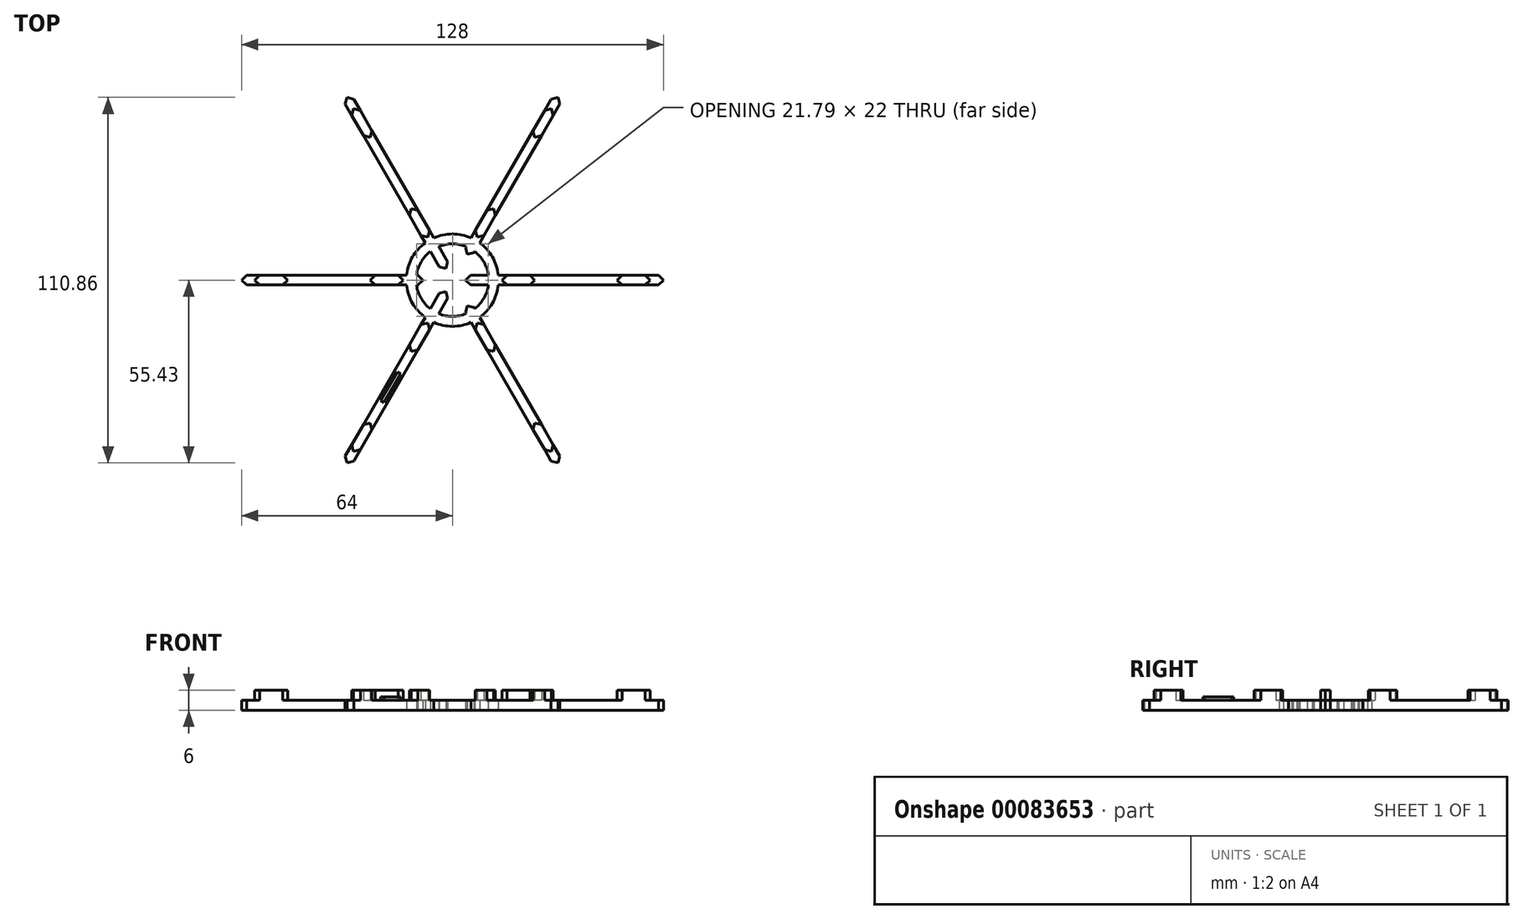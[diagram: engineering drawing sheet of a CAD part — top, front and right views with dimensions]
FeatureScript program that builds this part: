
annotation { "Feature Type Name" : "Feature", "Feature Type Description" : "" }
export const myFeature = defineFeature(function(context is Context, id is Id, definition is map)
    precondition{}
    {
        {
            var Q0;
            Q0=qCreatedBy(makeId("Top.planeOp"),FACE);
            var sketch = newSketch(context, id + "F0", { "sketchPlane" : qUnion([Q0])});
            skLineSegment(sketch, "E0", {"start": v(-51.99, 0) * mm, "end": v(34.37, 0) * mm, "construction": true});
            skLineSegment(sketch, "E1", {"start": v(-11.35, 19.65) * mm, "end": v(25.33, -43.88) * mm, "construction": true});
            skLineSegment(sketch, "E2", {"start": v(11.11, 19.25) * mm, "end": v(-29.6, -51.26) * mm, "construction": true});
            skLineSegment(sketch, "E3", {"start": v(-4.05, -4.01) * mm, "end": v(-32.55, -53.38) * mm});
            skLineSegment(sketch, "E4", {"start": v(-29.95, -54.88) * mm, "end": v(-1.45, -5.51) * mm});
            skCircle(sketch, "E5", {"center": v(0, 0) * mm, "radius": 4 * mm, "construction": true});
            skLineSegment(sketch, "E6", {"start": v(-4.05, -4.01) * mm, "end": v(-2, -3.46) * mm});
            skLineSegment(sketch, "E7", {"start": v(-2, -3.46) * mm, "end": v(-1.45, -5.51) * mm});
            skLineSegment(sketch, "E8", {"start": v(-32.55, -53.38) * mm, "end": v(-32, -55.43) * mm});
            skLineSegment(sketch, "E9", {"start": v(-32, -55.43) * mm, "end": v(-29.95, -54.88) * mm});
            skLineSegment(sketch, "E10", {"start": v(-62.5, 1.5) * mm, "end": v(-10.5, 1.5) * mm});
            skLineSegment(sketch, "E11", {"start": v(-10.5, -1.5) * mm, "end": v(-62.5, -1.5) * mm});
            skLineSegment(sketch, "E12", {"start": v(-10.5, 1.5) * mm, "end": v(-9, 0) * mm});
            skLineSegment(sketch, "E13", {"start": v(-9, 0) * mm, "end": v(-10.5, -1.5) * mm});
            skLineSegment(sketch, "E14", {"start": v(-62.5, 1.5) * mm, "end": v(-64, 0) * mm});
            skLineSegment(sketch, "E15", {"start": v(-64, 0) * mm, "end": v(-62.5, -1.5) * mm});
            skCircle(sketch, "E16", {"center": v(0, 0) * mm, "radius": 64 * mm, "construction": true});
            skSolve(sketch);
        }
        {
            var Q0;
            {var subQ0=sQuery(id+"F0.wireOp",EDGE,"c0tjFI8d-UXuB-YWxn-vJMP-8DVr5BACsfKR");var subQ1=sQuery(id+"F0.wireOp",EDGE,"E4");var subQ2=makeQuery(id+"F0.imprint","INTERSECT",VERTEX,{"derivedFrom":[subQ1,subQ0]});Q0=makeQuery(id+"F0.imprint","IMPRINT",FACE,{"disambiguationData":[TD([[makeQuery(id+"F0.imprint","IMPRINT",EDGE,{"disambiguationData":[TD([[subQ2,-1.0]])],"derivedFrom":subQ1}),-1.0]])]});}
            var Q1;
            {var subQ0=sQuery(id+"F0.wireOp",EDGE,"E6");Q1=makeQuery(id+"F0.imprint","IMPRINT",FACE,{"disambiguationData":[TD([[makeQuery(id+"F0.imprint","IMPRINT",EDGE,{"derivedFrom":subQ0}),-1.0]])]});}
            var Q2;
            {var subQ0=sQuery(id+"F0.wireOp",EDGE,"c0tjFI8d-UXuB-YWxn-vJMP-8DVr5BACsfKR");var subQ1=sQuery(id+"F0.wireOp",EDGE,"E3");var subQ2=makeQuery(id+"F0.imprint","INTERSECT",VERTEX,{"derivedFrom":[subQ1,subQ0]});Q2=makeQuery(id+"F0.imprint","IMPRINT",FACE,{"disambiguationData":[TD([[makeQuery(id+"F0.imprint","IMPRINT",EDGE,{"disambiguationData":[TD([[subQ2,1.0]])],"derivedFrom":subQ1}),1.0]])]});}
            var Q3;
            {var subQ0=sQuery(id+"F0.wireOp",EDGE,"c0tjFI8d-UXuB-YWxn-vJMP-8DVr5BACsfKR");var subQ1=sQuery(id+"F0.wireOp",EDGE,"E3");var subQ2=makeQuery(id+"F0.imprint","INTERSECT",VERTEX,{"derivedFrom":[subQ1,subQ0]});Q3=makeQuery(id+"F0.imprint","IMPRINT",FACE,{"disambiguationData":[TD([[makeQuery(id+"F0.imprint","IMPRINT",EDGE,{"disambiguationData":[TD([[subQ2,1.0]])],"derivedFrom":subQ1}),-1.0]])]});}
            var Q4;
            {var subQ0=sQuery(id+"F0.wireOp",EDGE,"E11");var subQ1=sQuery(id+"F0.wireOp",EDGE,"mBwGdOnb-4WHf-gQnb-HGub-ObEceEUmqNSN");var subQ2=makeQuery(id+"F0.imprint","INTERSECT",VERTEX,{"derivedFrom":[subQ1,subQ0]});Q4=makeQuery(id+"F0.imprint","IMPRINT",FACE,{"disambiguationData":[TD([[makeQuery(id+"F0.imprint","IMPRINT",EDGE,{"disambiguationData":[TD([[subQ2,1.0]])],"derivedFrom":subQ1}),-1.0]])]});}
            var Q5;
            {var subQ0=sQuery(id+"F0.wireOp",EDGE,"E12");Q5=makeQuery(id+"F0.imprint","IMPRINT",FACE,{"disambiguationData":[TD([[makeQuery(id+"F0.imprint","IMPRINT",EDGE,{"derivedFrom":subQ0}),-1.0]])]});}
            var Q6;
            {var subQ5=sQuery(id+"F0.wireOp",EDGE,"E8");Q6=makeQuery(id+"F0.imprint","IMPRINT",FACE,{"disambiguationData":[TD([[makeQuery(id+"F0.imprint","IMPRINT",EDGE,{"derivedFrom":subQ5}),1.0]])]});}
            var Q7;
            {var subQ4=sQuery(id+"F0.wireOp",EDGE,"E14");Q7=makeQuery(id+"F0.imprint","IMPRINT",FACE,{"disambiguationData":[TD([[makeQuery(id+"F0.imprint","IMPRINT",EDGE,{"derivedFrom":subQ4}),1.0]])]});}
            extrude(context, id + "F1", {"entities" : qUnion([Q0, Q1, Q2, Q3, Q4, Q5, Q6, Q7]), "depth" : 3 * mm});
        }
        {
            var Q0;
            Q0=qCreatedBy(makeId("Front.planeOp"),FACE);
            var sketch = newSketch(context, id + "F2", { "sketchPlane" : qUnion([Q0])});
            skLineSegment(sketch, "E17", {"start": v(0, 33.07) * mm, "end": v(0, -32.69) * mm, "construction": true});
            skSolve(sketch);
        }
        {
            var Q0;
            Q0=makeQuery(id+"F1.opExtrude","CAP_FACE",FACE,{"disambiguationData":[OSD([sQuery(id+"F0.wireOp",EDGE,"E3"),sQuery(id+"F0.wireOp",EDGE,"E4"),sQuery(id+"F0.wireOp",EDGE,"mBwGdOnb-4WHf-gQnb-HGub-ObEceEUmqNSN"),sQuery(id+"F0.wireOp",EDGE,"c0tjFI8d-UXuB-YWxn-vJMP-8DVr5BACsfKR"),sQuery(id+"F0.wireOp",EDGE,"E6"),sQuery(id+"F0.wireOp",EDGE,"E7"),sQuery(id+"F0.wireOp",EDGE,"E8"),sQuery(id+"F0.wireOp",EDGE,"E9"),sQuery(id+"F0.wireOp",EDGE,"E10"),sQuery(id+"F0.wireOp",EDGE,"E11"),sQuery(id+"F0.wireOp",EDGE,"E12"),sQuery(id+"F0.wireOp",EDGE,"E13"),sQuery(id+"F0.wireOp",EDGE,"E14"),sQuery(id+"F0.wireOp",EDGE,"E15")])],"isStart":false});
            var sketch = newSketch(context, id + "F3", { "sketchPlane" : qUnion([Q0])});
            skLineSegment(sketch, "E18", {"start": v(0, 0) * mm, "end": v(-72.83, 0) * mm, "construction": true});
            skLineSegment(sketch, "E19", {"start": v(-58.5, 1.5) * mm, "end": v(-51.5, 1.5) * mm});
            skLineSegment(sketch, "E20", {"start": v(-51.5, 1.5) * mm, "end": v(-50, 0) * mm});
            skLineSegment(sketch, "E21", {"start": v(-50, 0) * mm, "end": v(-51.5, -1.5) * mm});
            skLineSegment(sketch, "E22", {"start": v(-51.5, -1.5) * mm, "end": v(-58.5, -1.5) * mm});
            skLineSegment(sketch, "E23", {"start": v(-58.5, -1.5) * mm, "end": v(-60, 0) * mm});
            skLineSegment(sketch, "E24", {"start": v(-60, 0) * mm, "end": v(-58.5, 1.5) * mm});
            skLineSegment(sketch, "E25", {"start": v(-23.5, 1.5) * mm, "end": v(-16.5, 1.5) * mm});
            skLineSegment(sketch, "E26", {"start": v(-16.5, 1.5) * mm, "end": v(-15, 0) * mm});
            skLineSegment(sketch, "E27", {"start": v(-15, 0) * mm, "end": v(-16.5, -1.5) * mm});
            skLineSegment(sketch, "E28", {"start": v(-16.5, -1.5) * mm, "end": v(-23.5, -1.5) * mm});
            skLineSegment(sketch, "E29", {"start": v(-23.5, -1.5) * mm, "end": v(-25, 0) * mm});
            skLineSegment(sketch, "E30", {"start": v(-25, 0) * mm, "end": v(-23.5, 1.5) * mm});
            skCircle(sketch, "E31", {"center": v(0, 0) * mm, "radius": 60 * mm, "construction": true});
            skLineSegment(sketch, "E32", {"start": v(0, 0) * mm, "end": v(-34.5, -59.74) * mm, "construction": true});
            skLineSegment(sketch, "E33", {"start": v(-30.55, -49.91) * mm, "end": v(-27.05, -43.85) * mm});
            skLineSegment(sketch, "E34", {"start": v(-27.05, -43.85) * mm, "end": v(-25, -43.3) * mm});
            skLineSegment(sketch, "E35", {"start": v(-25, -43.3) * mm, "end": v(-24.45, -45.35) * mm});
            skLineSegment(sketch, "E36", {"start": v(-24.45, -45.35) * mm, "end": v(-27.95, -51.41) * mm});
            skLineSegment(sketch, "E37", {"start": v(-27.95, -51.41) * mm, "end": v(-30, -51.96) * mm});
            skLineSegment(sketch, "E38", {"start": v(-30, -51.96) * mm, "end": v(-30.55, -49.91) * mm});
            skLineSegment(sketch, "E39", {"start": v(-13.05, -19.6) * mm, "end": v(-9.55, -13.54) * mm});
            skLineSegment(sketch, "E40", {"start": v(-9.55, -13.54) * mm, "end": v(-7.5, -13) * mm});
            skLineSegment(sketch, "E41", {"start": v(-7.5, -13) * mm, "end": v(-6.95, -15.04) * mm});
            skLineSegment(sketch, "E42", {"start": v(-6.95, -15.04) * mm, "end": v(-10.45, -21.1) * mm});
            skLineSegment(sketch, "E43", {"start": v(-10.45, -21.1) * mm, "end": v(-12.5, -21.65) * mm});
            skLineSegment(sketch, "E44", {"start": v(-12.5, -21.65) * mm, "end": v(-13.05, -19.6) * mm});
            skSolve(sketch);
        }
        {
            var Q0;
            Q0=qSketchRegion(id+"F3",true);
            extrude(context, id + "F4", {"entities" : qUnion([Q0]), "operationType" : NewBodyOperationType.ADD, "depth" : 3 * mm});
        }
        {
            var Q0;
            Q0=makeQuery(id+"F1.opExtrude","SWEPT_BODY",BODY,{"disambiguationData":[OSD([sQuery(id+"F0.wireOp",EDGE,"E3"),sQuery(id+"F0.wireOp",EDGE,"E4"),sQuery(id+"F0.wireOp",EDGE,"mBwGdOnb-4WHf-gQnb-HGub-ObEceEUmqNSN"),sQuery(id+"F0.wireOp",EDGE,"c0tjFI8d-UXuB-YWxn-vJMP-8DVr5BACsfKR"),sQuery(id+"F0.wireOp",EDGE,"E6"),sQuery(id+"F0.wireOp",EDGE,"E7"),sQuery(id+"F0.wireOp",EDGE,"E8"),sQuery(id+"F0.wireOp",EDGE,"E9"),sQuery(id+"F0.wireOp",EDGE,"E10"),sQuery(id+"F0.wireOp",EDGE,"E11"),sQuery(id+"F0.wireOp",EDGE,"E12"),sQuery(id+"F0.wireOp",EDGE,"E13"),sQuery(id+"F0.wireOp",EDGE,"E14"),sQuery(id+"F0.wireOp",EDGE,"E15")])]});
            var Q1;
            Q1=sQuery(id+"F2.wireOp",EDGE,"E17");
            circularPattern(context, id + "F5", {"operationType" : NewBodyOperationType.ADD, "entities" : qUnion([Q0]), "axis" : qUnion([Q1]), "angle" : 120 * degree, "instanceCount" : 3});
        }
        {
            var Q0;
            {var subQ0=sQuery(id+"F0.wireOp",EDGE,"E8");var subQ1=sQuery(id+"F0.wireOp",EDGE,"E3");var subQ2=sQuery(id+"F0.wireOp",EDGE,"c0tjFI8d-UXuB-YWxn-vJMP-8DVr5BACsfKR");var subQ3=sQuery(id+"F0.wireOp",EDGE,"E9");var subQ4=sQuery(id+"F0.wireOp",EDGE,"E4");Q0=makeQuery(id+"F4.boolean.opBoolean","SPLIT",FACE,{"disambiguationData":[TD([makeQuery(id+"F4.opExtrude","SWEPT_FACE",FACE,{"disambiguationData":[OSD([sQuery(id+"F3.wireOp",EDGE,"E34")])]})])],"derivedFrom":makeQuery(id+"F1.opExtrude","CAP_FACE",FACE,{"disambiguationData":[OSD([subQ1,subQ4,sQuery(id+"F0.wireOp",EDGE,"mBwGdOnb-4WHf-gQnb-HGub-ObEceEUmqNSN"),subQ2,sQuery(id+"F0.wireOp",EDGE,"E6"),sQuery(id+"F0.wireOp",EDGE,"E7"),subQ0,subQ3,sQuery(id+"F0.wireOp",EDGE,"E10"),sQuery(id+"F0.wireOp",EDGE,"E11"),sQuery(id+"F0.wireOp",EDGE,"E12"),sQuery(id+"F0.wireOp",EDGE,"E13"),sQuery(id+"F0.wireOp",EDGE,"E14"),sQuery(id+"F0.wireOp",EDGE,"E15")])],"isStart":false})});}
            var sketch = newSketch(context, id + "F6", { "sketchPlane" : qUnion([Q0])});
            skLineSegment(sketch, "E45", {"start": v(-12.5, -21.65) * mm, "end": v(-25, -43.3) * mm, "construction": true});
            skLineSegment(sketch, "E46", {"start": v(-16.77, -27.85) * mm, "end": v(-21.77, -36.5) * mm});
            skLineSegment(sketch, "E47", {"start": v(-21.77, -36.5) * mm, "end": v(-20.73, -37.1) * mm});
            skLineSegment(sketch, "E48", {"start": v(-20.73, -37.1) * mm, "end": v(-15.73, -28.45) * mm});
            skLineSegment(sketch, "E49", {"start": v(-15.73, -28.45) * mm, "end": v(-16.77, -27.85) * mm});
            skSolve(sketch);
        }
        {
            var Q0;
            Q0=qSketchRegion(id+"F6",true);
            extrude(context, id + "F7", {"entities" : qUnion([Q0]), "operationType" : NewBodyOperationType.ADD, "depth" : 1 * mm});
        }
        {
            var Q0;
            Q0=qCreatedBy(makeId("Top.planeOp"),FACE);
            var sketch = newSketch(context, id + "F8", { "sketchPlane" : qUnion([Q0])});
            skCircle(sketch, "E50", {"center": v(0, 0) * mm, "radius": 11 * mm});
            skCircle(sketch, "E51", {"center": v(0, 0) * mm, "radius": 14 * mm});
            skSolve(sketch);
        }
        {
            var Q0;
            Q0=qSketchRegion(id+"F8",true);
            extrude(context, id + "F9", {"entities" : qUnion([Q0]), "operationType" : NewBodyOperationType.ADD, "depth" : 3 * mm});
        }
    });
